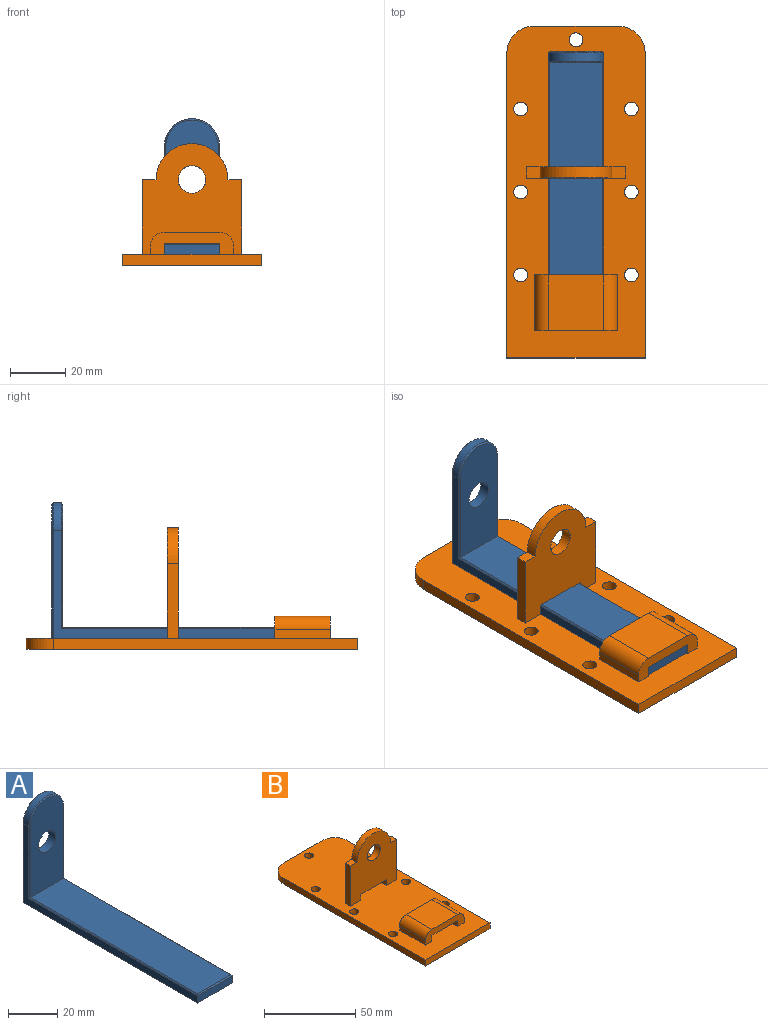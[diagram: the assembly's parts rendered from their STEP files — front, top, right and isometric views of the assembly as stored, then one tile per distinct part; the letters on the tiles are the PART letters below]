
ASSEMBLY  parts=2 mates=1
PART A: 18 faces, bbox 20x100x49 mm
  f0: plane 99.5x39mm, normal (-1,0,0), area 454.8mm2, adj f1,f5,f7,f11,f14,f16
  f1: plane 20x3.5mm, normal (0,-1,0), area 70mm2, adj f0,f2,f5,f12
  f2: plane 99.5x39mm, normal (1,0,0), area 454.8mm2, adj f1,f5,f7,f9,f13,f15
  f3: plane 48.5x19mm, normal (0,1,0), area 804.2mm2, adj f5,f8,f9,f10,f11
  f4: plane 95.5x19mm, normal (0,0,1), area 1814.5mm2, adj f6,f12,f13,f14
  f5: plane 100x20mm, normal (0,0,-1), area 1999.8mm2, adj f0,f1,f2,f3,f9,f11
  f6: plane 44.5x19mm, normal (0,-1,0), area 728.2mm2, adj f4,f8,f15,f16,f17
  f7: cylinder r=10mm len=20mm, axis (0,1,0), area 94.2mm2, adj f0,f2,f10,f17
  f8: cylinder r=5mm len=10mm, axis (0,1,0), area 125.7mm2, adj f3,f6
  f9: plane 39x0.5mm, normal (0.71,0.71,0), area 27.6mm2, adj f2,f3,f5,f10
  f10: cone r=9.5mm half-angle=45deg, axis (0,-1,0), area 21.7mm2, adj f3,f7,f9,f11
  f11: plane 39x0.5mm, normal (-0.71,0.71,0), area 27.6mm2, adj f0,f3,f5,f10
  f12: plane 20x0.5mm, normal (0,-0.71,0.71), area 13.8mm2, adj f1,f4,f13,f14
  f13: plane 96.5x0.5mm, normal (0.71,0,0.71), area 67.9mm2, adj f2,f4,f12,f15
  f14: plane 96.5x0.5mm, normal (-0.71,0,0.71), area 67.9mm2, adj f0,f4,f12,f16
  f15: plane 35.5x0.5mm, normal (0.71,-0.71,0), area 24.9mm2, adj f2,f6,f13,f17
  f16: plane 35.5x0.5mm, normal (-0.71,-0.71,0), area 24.9mm2, adj f0,f6,f14,f17
  f17: cone r=9.5mm half-angle=45deg, axis (0,1,0), area 21.7mm2, adj f6,f7,f15,f16
PART B: 36 faces, bbox 50x120x44 mm
  f0: plane 5x4mm, normal (0,0,1), area 20mm2, adj f1,f2,f20,f32
  f1: plane 40x36mm, normal (0,1,0), area 1078.9mm2, adj f0,f4,f19,f20,f21,f29,f30,f31
  f2: plane 40x36mm, normal (0,-1,0), area 1078.9mm2, adj f0,f4,f19,f20,f21,f29,f30,f31
  f3: plane 30x8mm, normal (0,1,0), area 149.3mm2, adj f4,f22,f24,f25,f26,f27,f28,f34
  f4: plane 120x50mm, normal (0,0,1), area 5555.6mm2, adj f1,f2,f3,f6,f7,f8,f9,f10
  f5: plane 120x50mm, normal (0,0,-1), area 5819.6mm2, adj f6,f7,f8,f9,f10,f11,f12,f13
  f6: plane 110x4mm, normal (-1,0,0), area 440mm2, adj f4,f5,f7,f11
  f7: plane 50x4mm, normal (0,-1,0), area 200mm2, adj f4,f5,f6,f8
  f8: plane 110x4mm, normal (1,0,0), area 440mm2, adj f4,f5,f7,f10
  f9: plane 30x4mm, normal (0,1,0), area 120mm2, adj f4,f5,f10,f11
  f10: cylinder r=10mm len=10mm, axis (0,0,1), area 62.8mm2, adj f4,f5,f8,f9
  f11: cylinder r=10mm len=10mm, axis (0,0,-1), area 62.8mm2, adj f4,f5,f6,f9
  f12: cylinder r=2.5mm len=5mm, axis (0,0,1), area 62.8mm2, adj f4,f5
  f13: cylinder r=2.5mm len=5mm, axis (0,0,1), area 62.8mm2, adj f4,f5
  f14: cylinder r=2.5mm len=5mm, axis (0,0,1), area 62.8mm2, adj f4,f5
  f15: cylinder r=2.5mm len=5mm, axis (0,0,1), area 62.8mm2, adj f4,f5
  f16: cylinder r=2.5mm len=5mm, axis (0,0,1), area 62.8mm2, adj f4,f5
  f17: cylinder r=2.5mm len=5mm, axis (0,0,1), area 62.8mm2, adj f4,f5
  f18: cylinder r=2.5mm len=5mm, axis (0,0,1), area 62.8mm2, adj f4,f5
  f19: plane 27x4mm, normal (-1,0,0), area 108mm2, adj f1,f2,f4,f21
  f20: plane 27x4mm, normal (1,0,0), area 108mm2, adj f0,f1,f2,f4
  f21: plane 5x4mm, normal (0,0,1), area 20mm2, adj f1,f2,f19,f32
  f22: plane 20x3mm, normal (-1,0,0), area 60mm2, adj f3,f4,f23,f34
  f23: plane 30x8mm, normal (0,-1,0), area 149.3mm2, adj f4,f22,f24,f25,f26,f27,f28,f34
  f24: plane 20x3mm, normal (1,0,0), area 60mm2, adj f3,f4,f23,f35
  f25: plane 20x20mm, normal (0,0,1), area 400mm2, adj f3,f23,f34,f35
  f26: plane 20x20mm, normal (0,0,-1), area 400mm2, adj f3,f23,f27,f28
  f27: plane 20x4mm, normal (-1,0,0), area 80mm2, adj f3,f4,f23,f26
  f28: plane 20x4mm, normal (1,0,0), area 80mm2, adj f3,f4,f23,f26
  f29: plane 4x4mm, normal (1,0,0), area 16mm2, adj f1,f2,f4,f31
  f30: plane 4x4mm, normal (-1,0,0), area 16mm2, adj f1,f2,f4,f31
  f31: plane 20x4mm, normal (0,0,-1), area 80mm2, adj f1,f2,f29,f30
  f32: cylinder r=13mm len=26mm, axis (0,-1,0), area 163.4mm2, adj f0,f1,f2,f21
  f33: cylinder r=5mm len=10mm, axis (0,-1,0), area 125.7mm2, adj f1,f2
  f34: cylinder r=5mm len=20mm, axis (0,1,0), area 157.1mm2, adj f3,f22,f23,f25
  f35: cylinder r=5mm len=20mm, axis (0,-1,0), area 157.1mm2, adj f3,f23,f24,f25
PLACE A t=(7.24,49.79,-6.2)mm
PLACE B t=(-7.76,39.06,-10.2)mm fixed
MATE fastened A.f5 <-> B.f4  axis (0,0,-1) through (17.24,99.78,-6.2)mm
